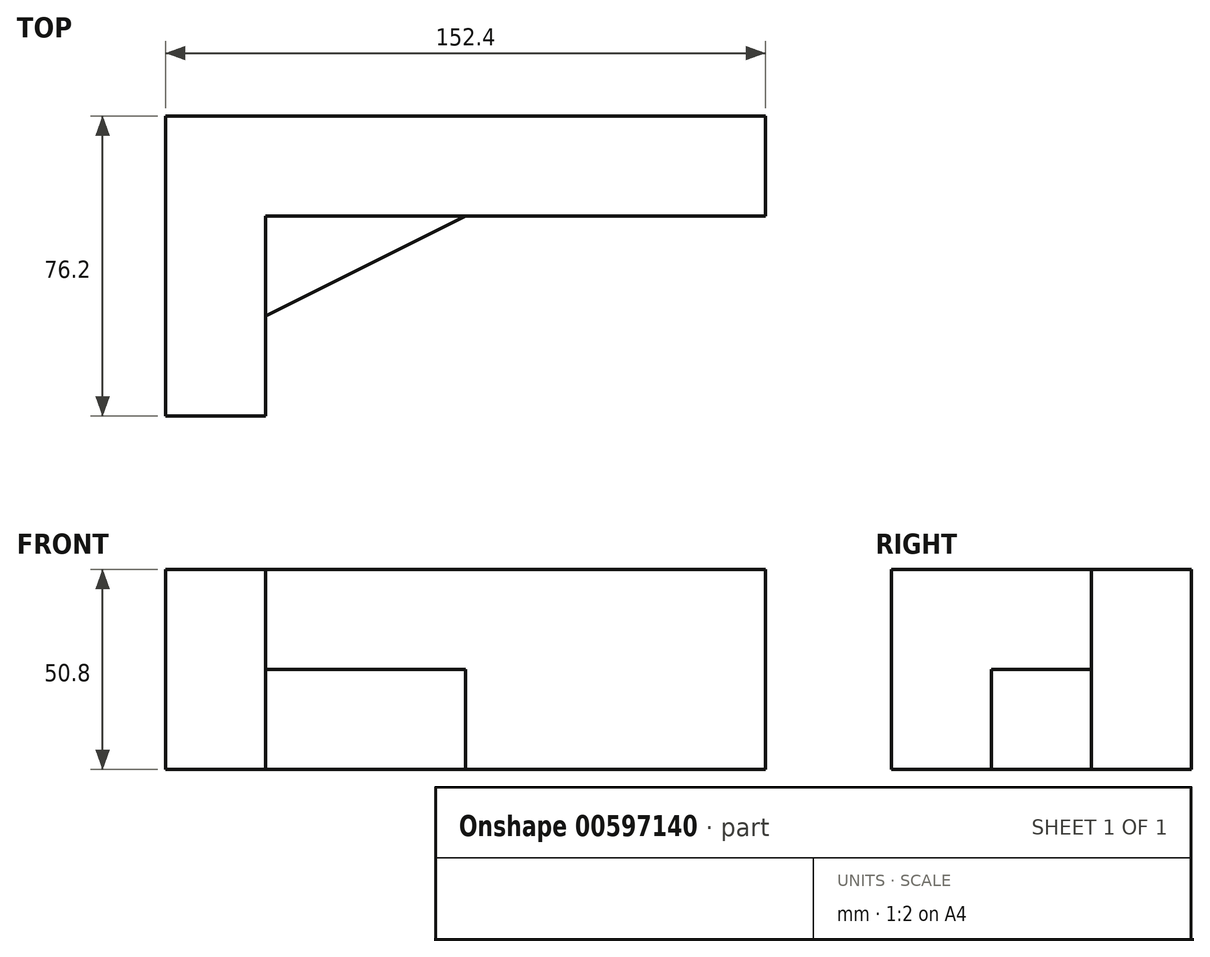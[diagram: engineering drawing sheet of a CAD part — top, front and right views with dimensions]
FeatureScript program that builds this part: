
annotation { "Feature Type Name" : "Feature", "Feature Type Description" : "" }
export const myFeature = defineFeature(function(context is Context, id is Id, definition is map)
    precondition{}
    {
        {
            var Q0;
            Q0=qCreatedBy(makeId("Front.planeOp"),FACE);
            var sketch = newSketch(context, id + "F0", { "sketchPlane" : qUnion([Q0])});
            skLineSegment(sketch, "E0.bottom", {"start": v(0, 0) * mm, "end": v(152.4, 0) * mm});
            skLineSegment(sketch, "E0.top", {"start": v(0, 50.8) * mm, "end": v(152.4, 50.8) * mm});
            skLineSegment(sketch, "E0.left", {"start": v(0, 0) * mm, "end": v(0, 50.8) * mm});
            skLineSegment(sketch, "E0.right", {"start": v(152.4, 0) * mm, "end": v(152.4, 50.8) * mm});
            skSolve(sketch);
        }
        {
            var Q0;
            Q0 = qSketchRegion(id + "F0", true);
            extrude(context, id + "F1", {"entities" : qUnion([Q0]), "oppositeDirection" : true, "depth" : 76.2 * mm, "offsetDistance" : 25.4 * mm});
        }
        {
            var Q0;
            Q0=makeQuery(id+"F1.opExtrude","CAP_FACE",FACE,{"disambiguationData":[OSD([sQuery(id+"F0.wireOp",EDGE,"E0.bottom"),sQuery(id+"F0.wireOp",EDGE,"E0.top"),sQuery(id+"F0.wireOp",EDGE,"E0.left"),sQuery(id+"F0.wireOp",EDGE,"E0.right")])],"isStart":true});
            var sketch = newSketch(context, id + "F2", { "sketchPlane" : qUnion([Q0])});
            skLineSegment(sketch, "E1", {"start": v(0, 50.8) * mm, "end": v(25.4, 50.8) * mm});
            skLineSegment(sketch, "E2", {"start": v(25.4, 50.8) * mm, "end": v(25.4, 0) * mm});
            skLineSegment(sketch, "E3", {"start": v(25.4, 0) * mm, "end": v(0, 0) * mm});
            skLineSegment(sketch, "E4", {"start": v(0, 0) * mm, "end": v(0, 50.8) * mm});
            skLineSegment(sketch, "E5", {"start": v(25.4, 50.8) * mm, "end": v(152.4, 50.8) * mm});
            skLineSegment(sketch, "E6", {"start": v(152.4, 50.8) * mm, "end": v(152.4, 0) * mm});
            skLineSegment(sketch, "E7", {"start": v(152.4, 0) * mm, "end": v(76.2, 0) * mm});
            skLineSegment(sketch, "E8", {"start": v(76.2, 0) * mm, "end": v(76.2, 25.4) * mm});
            skLineSegment(sketch, "E9", {"start": v(76.2, 25.4) * mm, "end": v(25.4, 25.4) * mm});
            skSolve(sketch);
        }
        {
            var Q0;
            {var subQ0=sQuery(id+"F2.wireOp",EDGE,"E5");Q0=makeQuery(id+"F2.imprint","IMPRINT",FACE,{"disambiguationData":[TD([[makeQuery(id+"F2.imprint","IMPRINT",EDGE,{"derivedFrom":subQ0}),-1.0]])]});}
            extrude(context, id + "F3", {"entities" : qUnion([Q0]), "operationType" : NewBodyOperationType.REMOVE, "oppositeDirection" : true, "depth" : 50.8 * mm, "offsetDistance" : 25.4 * mm});
        }
        {
            var Q0;
            Q0=makeQuery(id+"F3.boolean.opBoolean","COPY",FACE,{"derivedFrom":makeQuery(id+"F3.opExtrude","SWEPT_FACE",FACE,{"disambiguationData":[OSD([sQuery(id+"F2.wireOp",EDGE,"E9")])]})});
            var sketch = newSketch(context, id + "F4", { "sketchPlane" : qUnion([Q0])});
            skLineSegment(sketch, "E10", {"start": v(25.4, 0) * mm, "end": v(25.4, 25.4) * mm});
            skLineSegment(sketch, "E11", {"start": v(25.4, 25.4) * mm, "end": v(76.2, 50.8) * mm});
            skLineSegment(sketch, "E12", {"start": v(76.2, 50.8) * mm, "end": v(25.4, 50.8) * mm});
            skLineSegment(sketch, "E13", {"start": v(25.4, 50.8) * mm, "end": v(25.4, 25.4) * mm});
            skSolve(sketch);
        }
        {
            var Q0;
            Q0=makeQuery(id+"F4.imprint","IMPRINT",FACE,{"disambiguationData":[TD([[makeQuery(id+"F4.imprint","IMPRINT",EDGE,{"derivedFrom":sQuery(id+"F4.wireOp",EDGE,"E10")}),1.0]])]});
            extrude(context, id + "F5", {"entities" : qUnion([Q0]), "operationType" : NewBodyOperationType.REMOVE, "oppositeDirection" : true, "depth" : 25.4 * mm, "offsetDistance" : 25.4 * mm});
        }
    });
